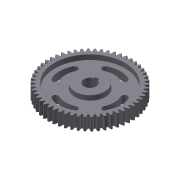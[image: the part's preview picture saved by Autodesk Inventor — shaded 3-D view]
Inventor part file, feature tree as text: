
AUTODESK INVENTOR PART (.ipt)
format: ipt  version: 2016 (Build 200138000, 138)  size: 429,568 bytes
history: native  units: mm (DEFAULTED — no unit token found)
features: sketch x6, extrude x5, plane x3, other x3, fillet x3, projected_geometry x2, pattern_circular x1
ambient origin geometry x8: Origin, YZ Plane, XZ Plane, XY Plane, X Axis, Y Axis, Z Axis, Center Point
bodies: Solid1 (feature_tree)
feature tree (23):
  extrude  "Extrusion1"  Depth=25.0mm TaperAngle=0.0deg
  plane  "Work Plane2"
  plane  "Work Plane8"
  plane  "Work Plane9"
  other  "Engranaje recto"
  extrude  "Extrusión2"  Depth=10.0mm TaperAngle=0.0deg
  extrude  "Extrusión3"  Depth=0.581776mm TaperAngle=0.0deg
  extrude  "Extrusión5"  TaperAngle=0.0deg  [1 undecoded]
  extrude  "Extrusión6"  Depth=108.0mm
  pattern_circular  "Patrón circular1"  Count=14  [1 undecoded]
  fillet  "Empalme1"  Radius=60.0mm
  fillet  "Empalme2"  Radius=10.0mm
  fillet  "Empalme3"  Radius=25.0mm
  sketch  "Sketch1"  dims[d0=168.0mm d1=25.0mm d2=0.0mm]
  sketch  "Sketch2"  dims[d3=162.0mm d4=10.0mm d5=0.0mm]
  other  "Srf1"
  sketch  "Boceto3"  dims[d16=108.0mm d17=0.0mm d34=0.581776mm]
  sketch  "Boceto4"  dims[d39=0.0mm d41=0.0mm]
  sketch  "Boceto6"  dims[d43=108.0mm d46=108.0mm]
  projected_geometry  "Contorno proyectado2"
  sketch  "Boceto7"  dims[d47=0.0mm d48=0.0mm d49=140.0mm d50=60.0mm d51=10.0mm d52=0.0mm d53=25.0mm d54=10.0mm d55=0.0mm d60=8.0mm d61=6.0mm d62=10.0mm d63=0.0mm d64=50.0mm d65=12.0mm d66=10.0mm d67=0.0mm d68=40.0mm d69=360.0deg d71=1.0mm d72=1.0mm d73=1.0mm]
  projected_geometry  "Contorno proyectado3"
  other  "Diámetro de separación"
note: 2 required parameter values undecoded (feature->parameter linkage not recoverable at this tier; creation-order binding heuristic only, values carry confidence <= 0.55)
